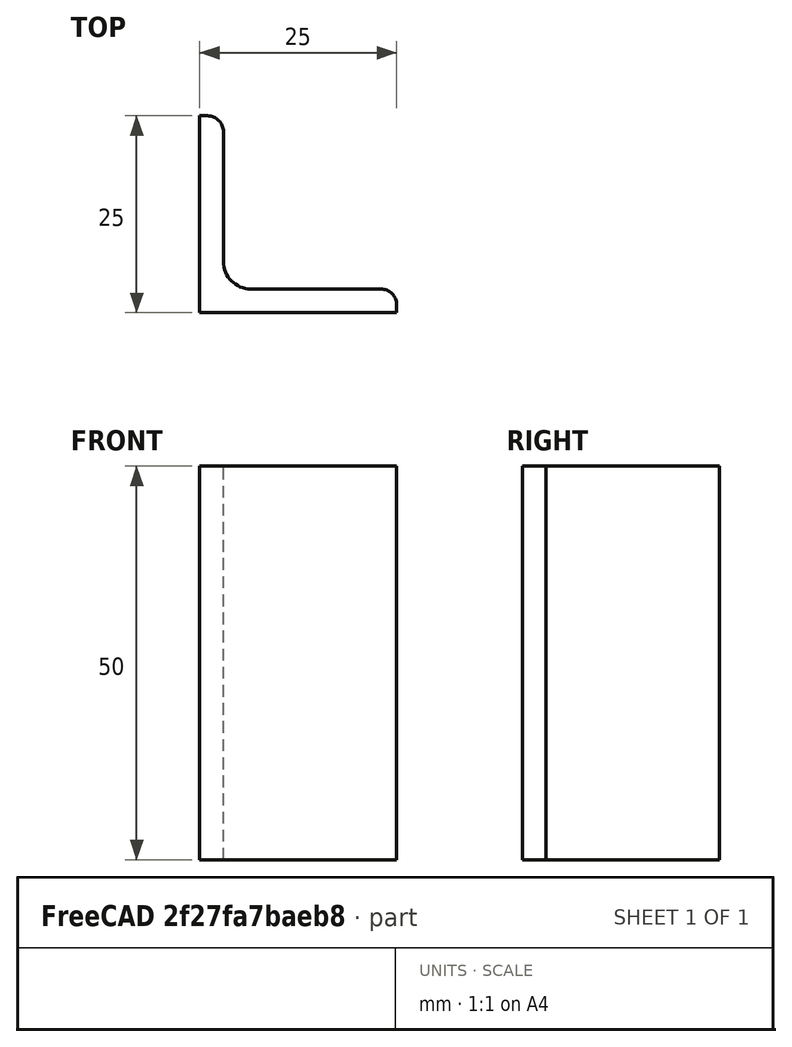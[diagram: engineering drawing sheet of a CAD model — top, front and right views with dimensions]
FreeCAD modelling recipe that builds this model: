
FCSTD DOCUMENT  (FreeCAD 0.15R4671 (Git))
Label: Angle Bar L25x25x3 EN10056 S235JR
License: All rights reserved
LicenseURL: http://en.wikipedia.org/wiki/All_rights_reserved
objects: Sketcher::SketchObject×1, Part::Extrusion×1
note: 2 computed .brp shape members not serialized (recipe doc carries the construction recipe); baked Part::Feature solids carry a one-line shape summary decoded from their .brp

FEATURE [Sketcher::SketchObject] Sketch
  sketch-geometry (9):
    g0: LineSegment StartX=0 StartY=0 StartZ=0 EndX=25 EndY=0 EndZ=0
    g1: LineSegment StartX=25 StartY=0 StartZ=0 EndX=25 EndY=1 EndZ=0
    g2: LineSegment StartX=23 StartY=3 StartZ=0 EndX=6.5 EndY=3 EndZ=0
    g3: LineSegment StartX=0 StartY=0 StartZ=0 EndX=0 EndY=25 EndZ=0
    g4: LineSegment StartX=0 StartY=25 StartZ=0 EndX=1 EndY=25 EndZ=0
    g5: LineSegment StartX=3 StartY=23 StartZ=0 EndX=3 EndY=6.5 EndZ=0
    g6: ArcOfCircle CenterX=6.5 CenterY=6.5 CenterZ=0 NormalX=0 NormalY=0 NormalZ=1 Radius=3.5 StartAngle=3.14159 EndAngle=4.71239
    g7: ArcOfCircle CenterX=1 CenterY=23 CenterZ=0 NormalX=0 NormalY=0 NormalZ=1 Radius=2 StartAngle=0 EndAngle=1.5708
    g8: ArcOfCircle CenterX=23 CenterY=1 CenterZ=0 NormalX=0 NormalY=0 NormalZ=1 Radius=2 StartAngle=0 EndAngle=1.5708
  constraints (23):
    c: Coincident(g0,g-1)
    c: Horizontal(g0)
    c: Coincident(g1,g0)
    c: Vertical(g1)
    c: Horizontal(g2)
    c: Coincident(g3,g-1)
    c: Vertical(g3)
    c: Coincident(g4,g3)
    c: Horizontal(g4)
    c: Vertical(g5)
    c: Tangent(g5,g6) = -1.5708
    c: Tangent(g2,g6) = 1.5708
    c: Tangent(g4,g7) = 1.5708
    c: Tangent(g5,g7) = 1.5708
    c: Tangent(g2,g8) = -1.5708
    c: Tangent(g1,g8) = -1.5708
    c: DistanceX(g0) = 25
    c: DistanceY(g3) = 25
    c: DistanceY(g0,g2) = 3
    c: DistanceX(g3,g5) = 3
    c: Radius(g6) = 3.5
    c: Radius(g8) = 2
    c: Radius(g7) = 2
FEATURE [Part::Extrusion] Extrude  label="Angle Bar L25x25x3 EN10056 S235JR"
  Base = -> Sketch
  Dir = (0,0,50)
  Solid = true
